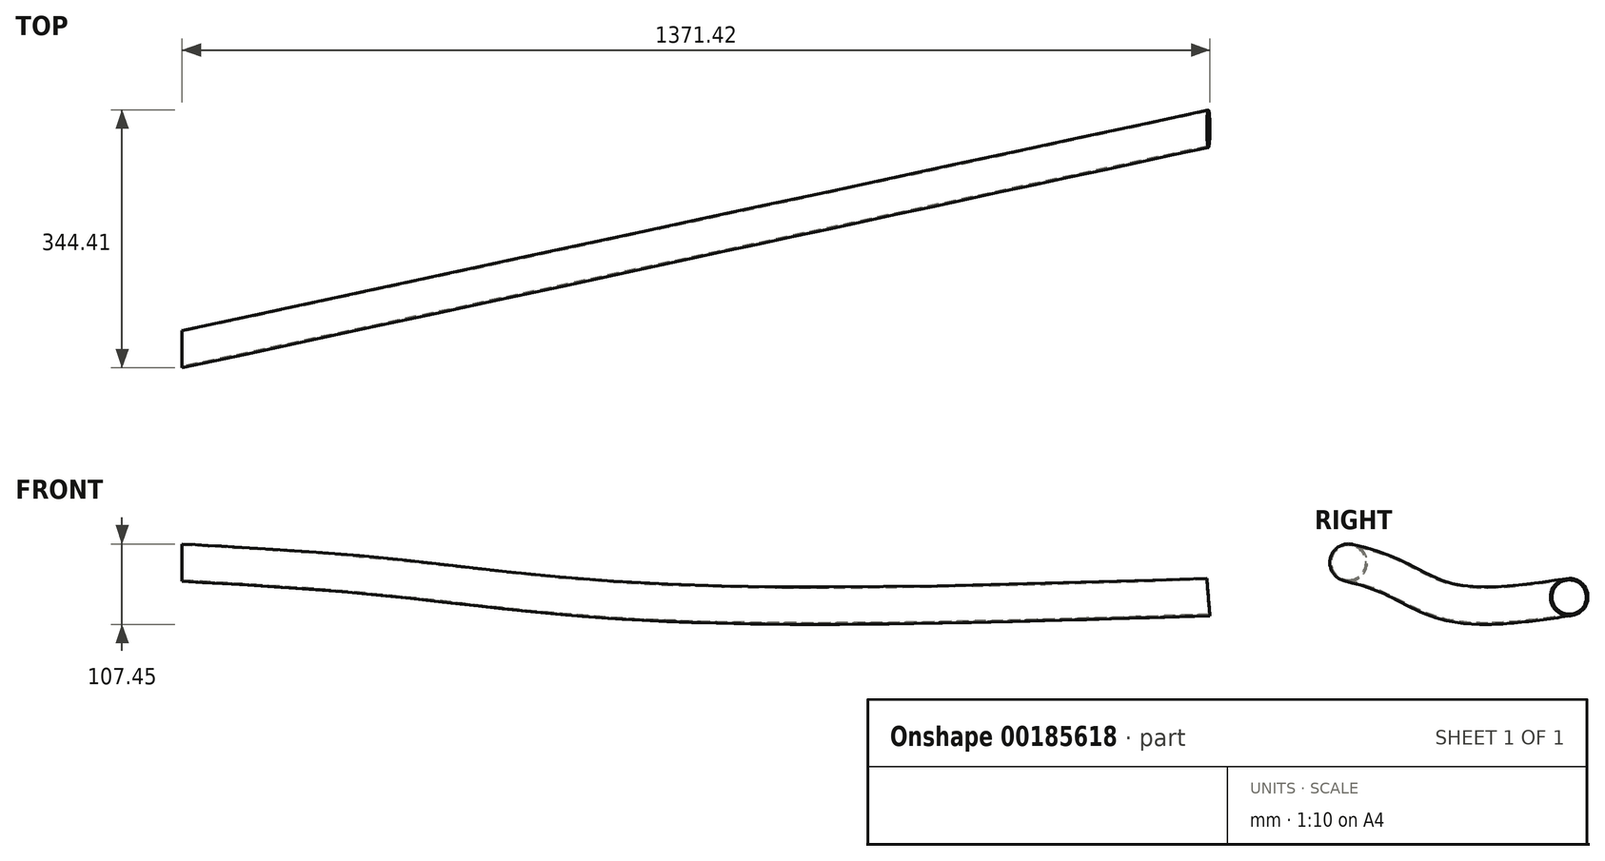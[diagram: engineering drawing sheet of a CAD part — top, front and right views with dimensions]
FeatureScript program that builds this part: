
annotation { "Feature Type Name" : "Feature", "Feature Type Description" : "" }
export const myFeature = defineFeature(function(context is Context, id is Id, definition is map)
    precondition{}
    {
        {
            var Q0;
            Q0=qCreatedBy(makeId("Top.planeOp"),FACE);
            var sketch = newSketch(context, id + "F0", { "sketchPlane" : qUnion([Q0])});
            skPoint(sketch, "E0", {"position": v(0, 0) * mm});
            skPoint(sketch, "E1", {"position": v(1369.35, 0) * mm});
            skPoint(sketch, "E2", {"position": v(1369.35, 294.42) * mm});
            skSolve(sketch);
        }
        {
            var Q0;
            Q0=sQuery(id+"F0.wireOp",VERTEX,"E2");
            var Q1;
            Q1=qCreatedBy(makeId("Front.planeOp"),FACE);
            cPlane(context, id + "F1", {"entities" : qUnion([Q0, Q1]), "cplaneType" : CPlaneType.PLANE_POINT, "offset" : 25 * mm, "width" : 150 * mm, "height" : 150 * mm});
        }
        {
            var Q0;
            Q0=qCreatedBy(id+"F1.planeOp",FACE);
            var sketch = newSketch(context, id + "F2", { "sketchPlane" : qUnion([Q0])});
            skPoint(sketch, "E3.0", {"position": v(1369.35, 0) * mm});
            skPoint(sketch, "E4", {"position": v(1369.35, -46) * mm});
            skSolve(sketch);
        }
        {
            var Q0;
            Q0=sQuery(id+"F0.wireOp",VERTEX,"E0");
            var Q1;
            Q1=sQuery(id+"F2.wireOp",VERTEX,"E4");
            var Q2;
            Q2=sQuery(id+"F0.wireOp",VERTEX,"E2");
            cPlane(context, id + "F3", {"entities" : qUnion([Q0, Q1, Q2]), "cplaneType" : CPlaneType.THREE_POINT, "offset" : 25 * mm, "width" : 150 * mm, "height" : 150 * mm});
        }
        {
            var Q0;
            Q0=qCreatedBy(makeId("Right.planeOp"),FACE);
            var sketch = newSketch(context, id + "F4", { "sketchPlane" : qUnion([Q0])});
            skCircle(sketch, "E5", {"center": v(0, 0) * mm, "radius": 25 * mm});
            skCircle(sketch, "E6.0", {"center": v(0, 0) * mm, "radius": 23 * mm});
            skSolve(sketch);
        }
        {
            var Q0;
            Q0=qCreatedBy(id+"F3.planeOp",FACE);
            var sketch = newSketch(context, id + "F5", { "sketchPlane" : qUnion([Q0])});
            skPoint(sketch, "E7.0", {"position": v(-1400.64, -46) * mm});
            skPoint(sketch, "E8.0", {"position": v(0, 0) * mm});
            skFitSpline(sketch, "E9", {"points": [v(0, 0) * mm, v(-272.9, -18.73) * mm, v(-642.46, -52.8) * mm, v(-1400.64, -46) * mm], "startDerivative": vector(-1030.2, -55.46) * mm, "endDerivative": vector(-1894.51, 58.79) * mm});
            skSolve(sketch);
        }
        {
            var Q0;
            Q0=makeQuery(id+"F4.imprint","IMPRINT",FACE,{"disambiguationData":[TD([[makeQuery(id+"F4.imprint","IMPRINT",EDGE,{"derivedFrom":sQuery(id+"F4.wireOp",EDGE,"E5")}),1.0]])]});
            var Q1;
            Q1=sQuery(id+"F5.wireOp",EDGE,"E9");
            sweep(context, id + "F6", {"profiles" : qUnion([Q0]), "path" : qUnion([Q1])});
        }
    });
